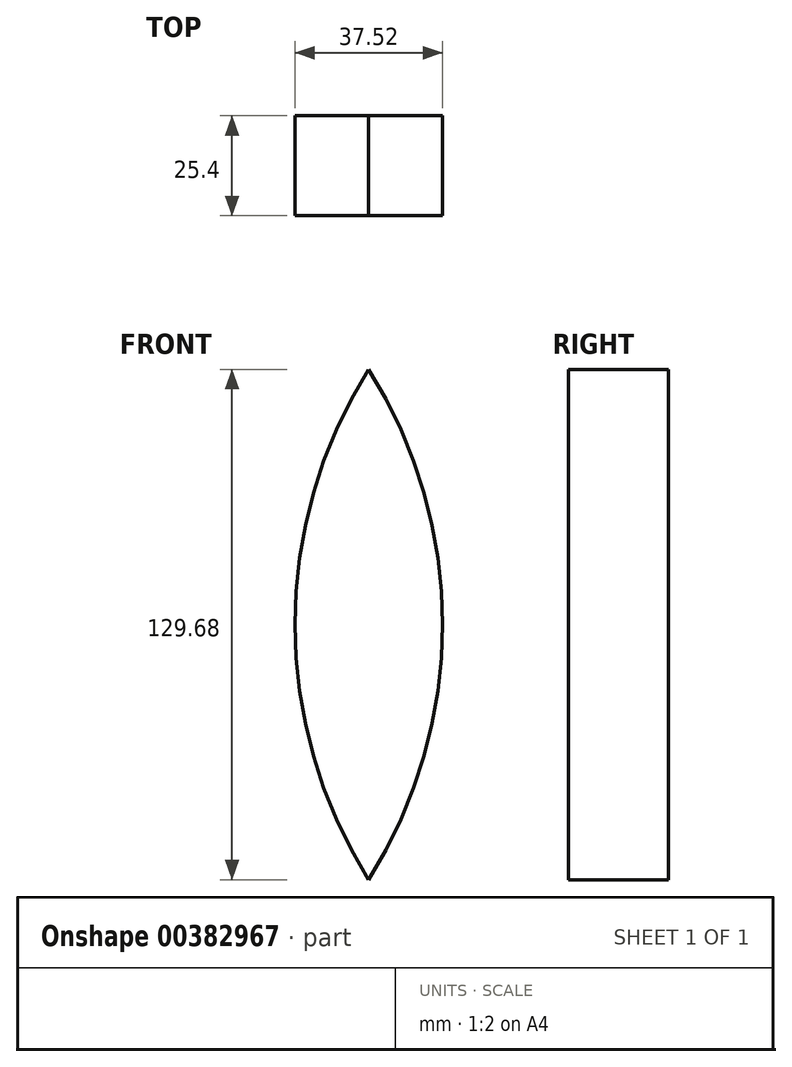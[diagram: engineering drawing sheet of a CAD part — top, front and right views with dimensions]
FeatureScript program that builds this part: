
annotation { "Feature Type Name" : "Feature", "Feature Type Description" : "" }
export const myFeature = defineFeature(function(context is Context, id is Id, definition is map)
    precondition{}
    {
        {
            var Q0;
            Q0=qCreatedBy(makeId("Front.planeOp"),FACE);
            var sketch = newSketch(context, id + "F0", { "sketchPlane" : qUnion([Q0])});
            skLineSegment(sketch, "E0.bottom", {"start": v(-18.76, 64.84) * mm, "end": v(18.76, 64.84) * mm});
            skLineSegment(sketch, "E0.top", {"start": v(-18.76, -64.84) * mm, "end": v(18.76, -64.84) * mm});
            skLineSegment(sketch, "E0.left", {"start": v(-18.76, 64.84) * mm, "end": v(-18.76, -64.84) * mm});
            skLineSegment(sketch, "E0.right", {"start": v(18.76, 64.84) * mm, "end": v(18.76, -64.84) * mm});
            skPoint(sketch, "E0.middle", {"position": v(0, 0) * mm});
            skArc(sketch, "E1", {"start": v(0, 64.84) * mm, "mid": v(-18.76, 0) * mm, "end": v(0, -64.84) * mm});
            skLineSegment(sketch, "E2", {"start": v(0, 64.84) * mm, "end": v(0, -64.84) * mm});
            skArc(sketch, "E3.MirrorCS", {"start": v(0, 64.84) * mm, "mid": v(18.76, 0) * mm, "end": v(0, -64.84) * mm});
            skLineSegment(sketch, "E4.MirrorCS", {"start": v(18.76, 64.84) * mm, "end": v(-18.76, 64.84) * mm});
            skSolve(sketch);
        }
        {
            var Q0;
            {var subQ1=sQuery(id+"F0.wireOp",EDGE,"E2");Q0=makeQuery(id+"F0.imprint","IMPRINT",FACE,{"disambiguationData":[TD([[makeQuery(id+"F0.imprint","IMPRINT",EDGE,{"derivedFrom":subQ1}),-1.0]])]});}
            var Q1;
            {var subQ0=sQuery(id+"F0.wireOp",EDGE,"E2");Q1=makeQuery(id+"F0.imprint","IMPRINT",FACE,{"disambiguationData":[TD([[makeQuery(id+"F0.imprint","IMPRINT",EDGE,{"derivedFrom":subQ0}),1.0]])]});}
            extrude(context, id + "F1", {"entities" : qUnion([Q0, Q1]), "depth" : 25.4 * mm});
        }
    });
